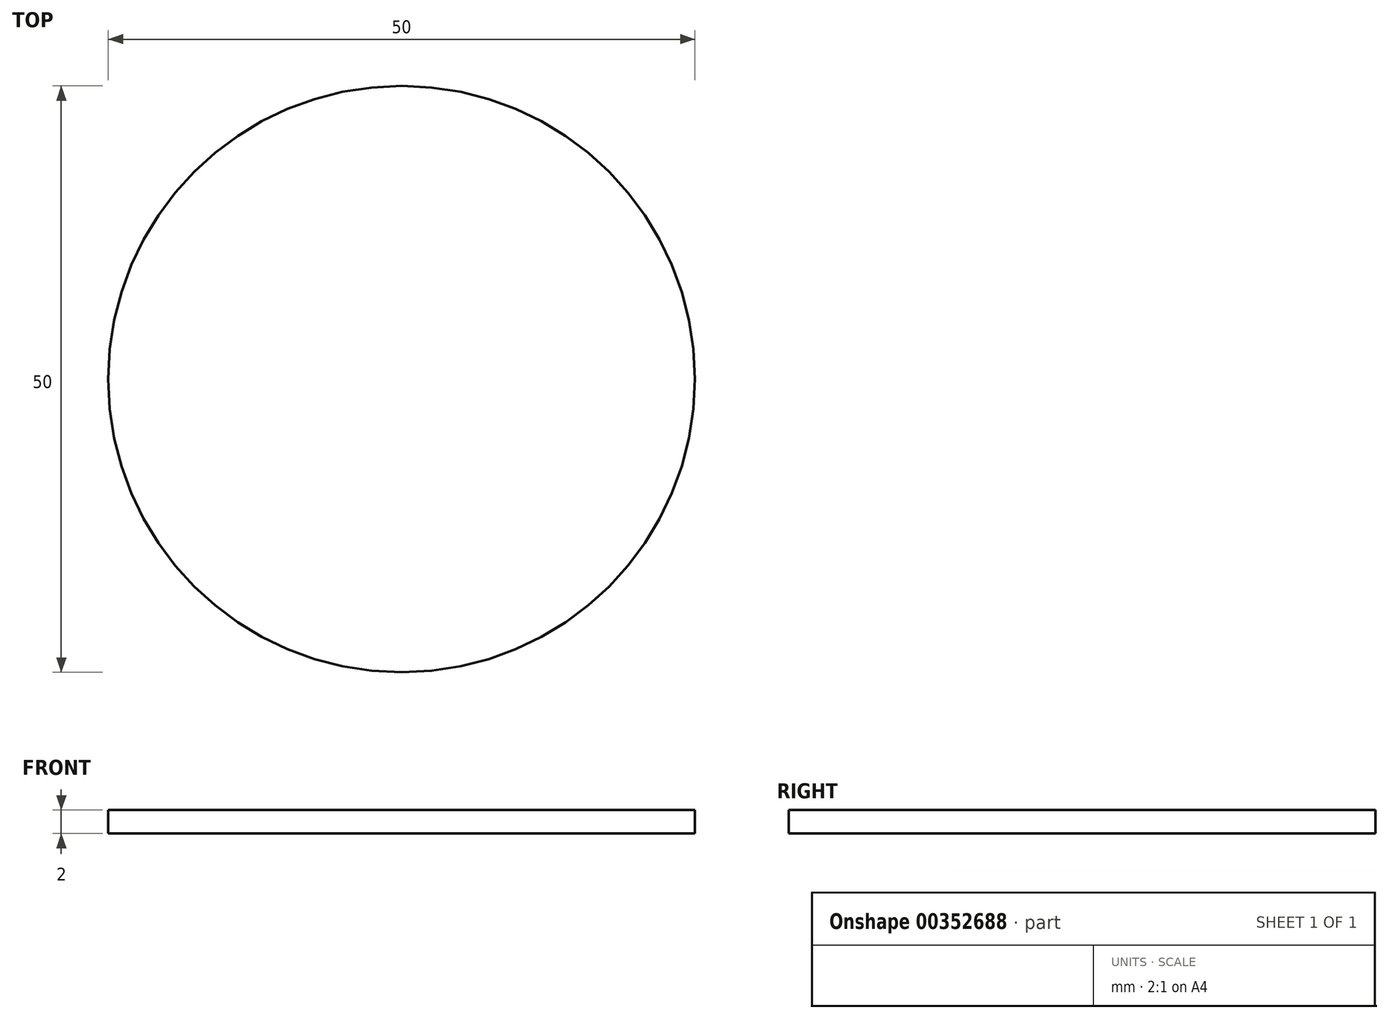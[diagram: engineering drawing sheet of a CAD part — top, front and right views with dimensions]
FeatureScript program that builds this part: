
annotation { "Feature Type Name" : "Feature", "Feature Type Description" : "" }
export const myFeature = defineFeature(function(context is Context, id is Id, definition is map)
    precondition{}
    {
        {
            var Q0;
            Q0=qCreatedBy(makeId("Top.planeOp"),FACE);
            var sketch = newSketch(context, id + "F0", { "sketchPlane" : qUnion([Q0])});
            skCircle(sketch, "E0", {"center": v(0, 0) * mm, "radius": 25 * mm});
            skSolve(sketch);
        }
        {
            var Q0;
            Q0=makeQuery(id+"F0.imprint","IMPRINT",FACE,{"disambiguationData":[TD([[makeQuery(id+"F0.imprint","IMPRINT",EDGE,{"derivedFrom":sQuery(id+"F0.wireOp",EDGE,"E0")}),1.0]])]});
            extrude(context, id + "F1", {"entities" : qUnion([Q0]), "depth" : 2 * mm});
        }
    });
